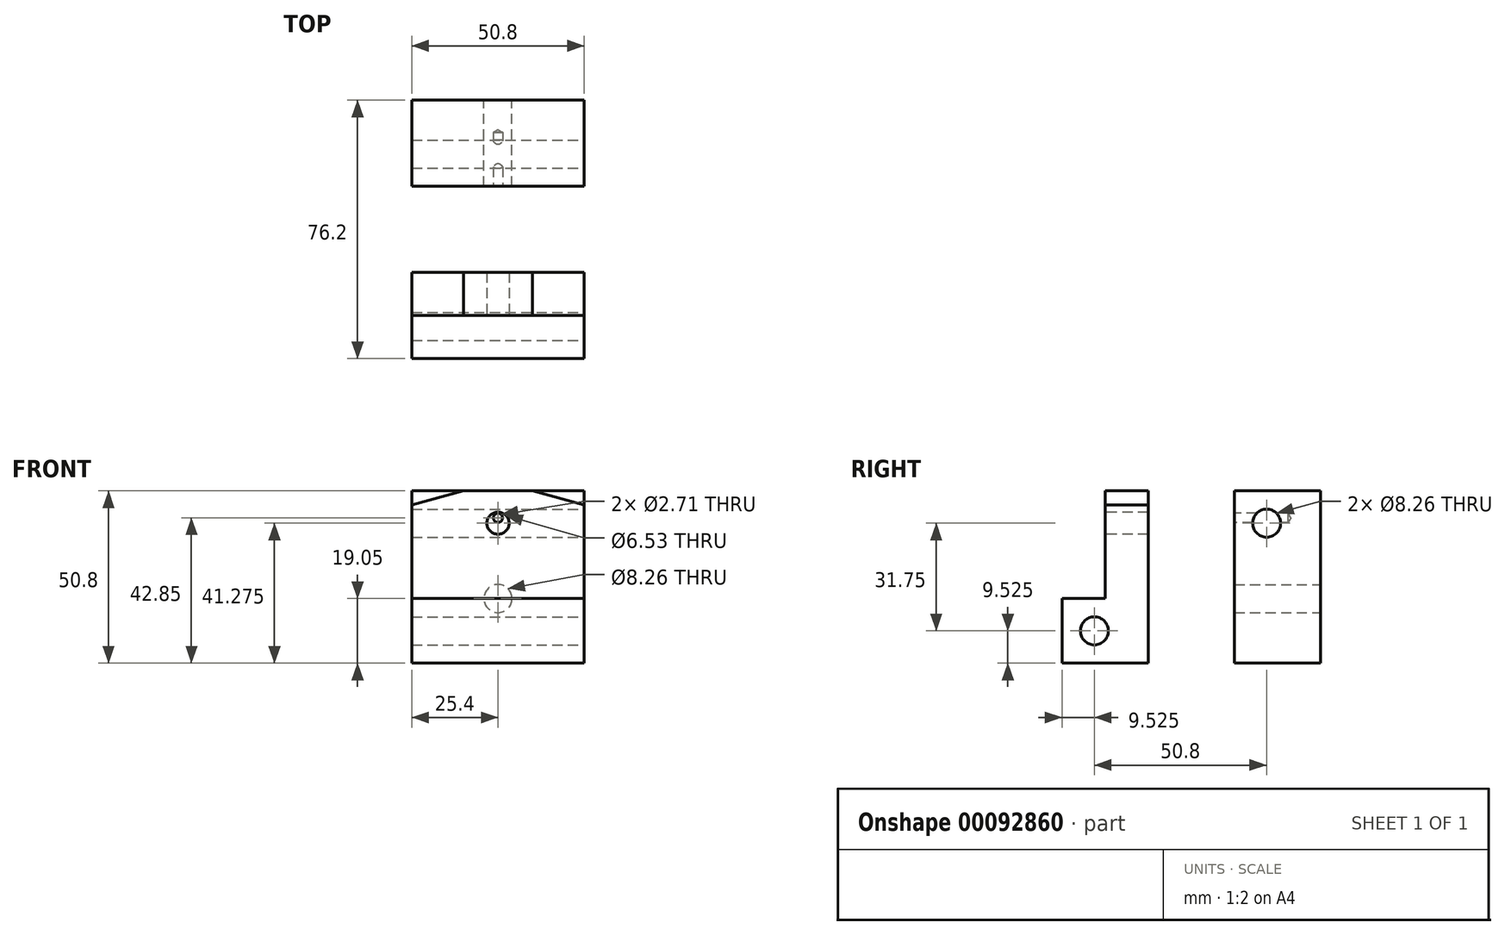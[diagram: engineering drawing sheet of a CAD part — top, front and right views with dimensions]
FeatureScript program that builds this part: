
annotation { "Feature Type Name" : "Feature", "Feature Type Description" : "" }
export const myFeature = defineFeature(function(context is Context, id is Id, definition is map)
    precondition{}
    {
        {
            var Q0;
            Q0=qCreatedBy(makeId("Front.planeOp"),FACE);
            var sketch = newSketch(context, id + "F0", { "sketchPlane" : qUnion([Q0])});
            skLineSegment(sketch, "E0.bottom", {"start": v(25.4, -25.4) * mm, "end": v(-25.4, -25.4) * mm});
            skLineSegment(sketch, "E0.top", {"start": v(25.4, 25.4) * mm, "end": v(-25.4, 25.4) * mm});
            skLineSegment(sketch, "E0.left", {"start": v(25.4, -25.4) * mm, "end": v(25.4, 25.4) * mm});
            skLineSegment(sketch, "E0.right", {"start": v(-25.4, -25.4) * mm, "end": v(-25.4, 25.4) * mm});
            skPoint(sketch, "E0.middle", {"position": v(0, 0) * mm});
            skLineSegment(sketch, "E1", {"start": v(-25.4, -6.35) * mm, "end": v(25.4, -6.35) * mm, "construction": true});
            skLineSegment(sketch, "E2", {"start": v(0, 25.4) * mm, "end": v(0, -25.4) * mm, "construction": true});
            skCircle(sketch, "E3", {"center": v(0, -6.35) * mm, "radius": 4.13 * mm});
            skSolve(sketch);
        }
        {
            var Q0;
            Q0=makeQuery(id+"F0.imprint","IMPRINT",FACE,{"disambiguationData":[TD([[makeQuery(id+"F0.imprint","IMPRINT",EDGE,{"derivedFrom":sQuery(id+"F0.wireOp",EDGE,"E0.bottom")}),-1.0]])]});
            extrude(context, id + "F1", {"entities" : qUnion([Q0]), "depth" : 25.4 * mm});
        }
        {
            var Q0;
            Q0=makeQuery(id+"F1.opExtrude","SWEPT_FACE",FACE,{"disambiguationData":[OSD([sQuery(id+"F0.wireOp",EDGE,"E0.left")])]});
            var sketch = newSketch(context, id + "F2", { "sketchPlane" : qUnion([Q0])});
            skLineSegment(sketch, "E4", {"start": v(-15.88, 25.4) * mm, "end": v(-15.87, -25.4) * mm, "construction": true});
            skLineSegment(sketch, "E5", {"start": v(-25.4, 15.88) * mm, "end": v(0, 15.88) * mm, "construction": true});
            skPoint(sketch, "E6", {"position": v(-15.88, 15.88) * mm});
            skSolve(sketch);
        }
        {
            var Q0;
            Q0=sQuery(id+"F2.wireOp",VERTEX,"E6");
            var Q1;
            Q1=makeQuery(id+"F1.opExtrude","SWEPT_BODY",BODY,{"disambiguationData":[OSD([sQuery(id+"F0.wireOp",EDGE,"E0.bottom"),sQuery(id+"F0.wireOp",EDGE,"E0.top"),sQuery(id+"F0.wireOp",EDGE,"E0.left"),sQuery(id+"F0.wireOp",EDGE,"E0.right"),sQuery(id+"F0.wireOp",EDGE,"E3")])]});
            hole(context, id + "F3", {"style" : HoleStyle.SIMPLE, "endStyle" : HoleEndStyle.THROUGH, "holeDiameter" : 8.25 * mm, "locations" : qUnion([Q0]), "scope" : qUnion([Q1]), "isTappedThrough" : true});
        }
        {
            var Q0;
            Q0=makeQuery(id+"F1.opExtrude","CAP_FACE",FACE,{"disambiguationData":[OSD([sQuery(id+"F0.wireOp",EDGE,"E0.bottom"),sQuery(id+"F0.wireOp",EDGE,"E0.top"),sQuery(id+"F0.wireOp",EDGE,"E0.left"),sQuery(id+"F0.wireOp",EDGE,"E0.right"),sQuery(id+"F0.wireOp",EDGE,"E3")])],"isStart":false});
            cPlane(context, id + "F4", {"entities" : qUnion([Q0]), "cplaneType" : CPlaneType.OFFSET, "offset" : 25.4 * mm, "width" : 152.4 * mm, "height" : 152.4 * mm});
        }
        {
            var Q0;
            Q0=qCreatedBy(id+"F4.planeOp",FACE);
            var sketch = newSketch(context, id + "F5", { "sketchPlane" : qUnion([Q0])});
            skLineSegment(sketch, "E7.0", {"start": v(10.16, 25.4) * mm, "end": v(-10.16, 25.4) * mm});
            skLineSegment(sketch, "E8.0", {"start": v(25.4, -25.4) * mm, "end": v(25.4, 21.32) * mm});
            skLineSegment(sketch, "E9.0", {"start": v(25.4, -25.4) * mm, "end": v(-25.4, -25.4) * mm});
            skLineSegment(sketch, "E10.0", {"start": v(-25.4, -25.4) * mm, "end": v(-25.4, 21.32) * mm});
            skLineSegment(sketch, "E11", {"start": v(0, 25.4) * mm, "end": v(0, -25.4) * mm, "construction": true});
            skLineSegment(sketch, "E12", {"start": v(-10.16, 25.4) * mm, "end": v(-10.16, -25.4) * mm, "construction": true});
            skLineSegment(sketch, "E13", {"start": v(-25.4, 15.87) * mm, "end": v(25.4, 15.88) * mm, "construction": true});
            skLineSegment(sketch, "E14", {"start": v(10.16, 25.4) * mm, "end": v(10.16, -25.4) * mm, "construction": true});
            skLineSegment(sketch, "E15", {"start": v(10.16, 25.4) * mm, "end": v(25.4, 21.32) * mm});
            skLineSegment(sketch, "E16", {"start": v(-10.16, 25.4) * mm, "end": v(-25.4, 21.32) * mm});
            skPoint(sketch, "E17", {"position": v(0, 15.88) * mm});
            skPoint(sketch, "E18.orphan", {"position": v(-25.4, 25.4) * mm});
            skPoint(sketch, "E19.orphan", {"position": v(25.4, 25.4) * mm});
            skSolve(sketch);
        }
        {
            var Q0;
            Q0=makeQuery(id+"F5.imprint","IMPRINT",FACE,{"disambiguationData":[TD([[makeQuery(id+"F5.imprint","IMPRINT",EDGE,{"derivedFrom":sQuery(id+"F5.wireOp",EDGE,"E7.0")}),1.0]])]});
            extrude(context, id + "F6", {"entities" : qUnion([Q0]), "depth" : 25.4 * mm});
        }
        {
            var Q0;
            Q0=makeQuery(id+"F6.opExtrude","CAP_FACE",FACE,{"disambiguationData":[OSD([sQuery(id+"F5.wireOp",EDGE,"E7.0"),sQuery(id+"F5.wireOp",EDGE,"E8.0"),sQuery(id+"F5.wireOp",EDGE,"E9.0"),sQuery(id+"F5.wireOp",EDGE,"E10.0"),sQuery(id+"F5.wireOp",EDGE,"E15"),sQuery(id+"F5.wireOp",EDGE,"E16")])],"isStart":false});
            var sketch = newSketch(context, id + "F7", { "sketchPlane" : qUnion([Q0])});
            skPoint(sketch, "E20.0", {"position": v(0, 15.88) * mm});
            skSolve(sketch);
        }
        {
            var Q0;
            Q0=sQuery(id+"F7.wireOp",VERTEX,"E20.0");
            var Q1;
            Q1=makeQuery(id+"F6.opExtrude","SWEPT_BODY",BODY,{"disambiguationData":[OSD([sQuery(id+"F5.wireOp",EDGE,"E7.0"),sQuery(id+"F5.wireOp",EDGE,"E8.0"),sQuery(id+"F5.wireOp",EDGE,"E9.0"),sQuery(id+"F5.wireOp",EDGE,"E10.0"),sQuery(id+"F5.wireOp",EDGE,"E15"),sQuery(id+"F5.wireOp",EDGE,"E16")])]});
            hole(context, id + "F8", {"style" : HoleStyle.SIMPLE, "endStyle" : HoleEndStyle.THROUGH, "standardTappedOrClearance" : lookupTablePath({ "standard" : "ANSI", "engagement" : "75%", "pitch" : "18 tpi", "size" : "5/16", "type" : "Tapped" }), "standardBlindInLast" : lookupTablePath({ "standard" : "ANSI", "engagement" : "75%", "pitch" : "18 tpi", "size" : "5/16", "type" : "Tapped" }), "holeDiameter" : 6.53 * mm, "locations" : qUnion([Q0]), "scope" : qUnion([Q1]), "isTappedThrough" : true, "majorDiameter" : 7.94 * mm, "showTappedDepth" : true});
        }
        {
            var Q0;
            Q0=makeQuery(id+"F6.opExtrude","SWEPT_FACE",FACE,{"disambiguationData":[OSD([sQuery(id+"F5.wireOp",EDGE,"E8.0")])]});
            var sketch = newSketch(context, id + "F9", { "sketchPlane" : qUnion([Q0])});
            skLineSegment(sketch, "E21.0", {"start": v(-76.2, 25.4) * mm, "end": v(-50.8, 25.4) * mm, "construction": true});
            skLineSegment(sketch, "E22.0", {"start": v(-76.2, -25.4) * mm, "end": v(-76.2, 21.32) * mm, "construction": true});
            skLineSegment(sketch, "E23.0", {"start": v(-76.2, 25.4) * mm, "end": v(-76.2, 21.32) * mm, "construction": true});
            skLineSegment(sketch, "E24.0", {"start": v(-76.2, -25.4) * mm, "end": v(-50.8, -25.4) * mm, "construction": true});
            skLineSegment(sketch, "E25.0", {"start": v(-50.8, -25.4) * mm, "end": v(-50.8, 21.32) * mm, "construction": true});
            skLineSegment(sketch, "E26.0.0", {"start": v(-50.8, 21.32) * mm, "end": v(-50.8, 25.4) * mm, "construction": true});
            skLineSegment(sketch, "E26.0.1", {"start": v(-50.8, 25.4) * mm, "end": v(-76.2, 25.4) * mm, "construction": true});
            skLineSegment(sketch, "E26.0.3", {"start": v(-76.2, 21.32) * mm, "end": v(-50.8, 21.32) * mm, "construction": true});
            skLineSegment(sketch, "E27", {"start": v(-63.5, 25.4) * mm, "end": v(-63.5, -25.4) * mm, "construction": true});
            skLineSegment(sketch, "E28", {"start": v(-76.2, -6.35) * mm, "end": v(-50.8, -6.35) * mm, "construction": true});
            skLineSegment(sketch, "E29.bottom", {"start": v(-76.2, 25.4) * mm, "end": v(-63.5, 25.4) * mm});
            skLineSegment(sketch, "E29.top", {"start": v(-76.2, -6.35) * mm, "end": v(-63.5, -6.35) * mm});
            skLineSegment(sketch, "E29.left", {"start": v(-76.2, 25.4) * mm, "end": v(-76.2, -6.35) * mm});
            skLineSegment(sketch, "E29.right", {"start": v(-63.5, 25.4) * mm, "end": v(-63.5, -6.35) * mm});
            skSolve(sketch);
        }
        {
            var Q0;
            {var subQ0=sQuery(id+"F9.wireOp",EDGE,"E29.top");Q0=makeQuery(id+"F9.imprint","IMPRINT",FACE,{"disambiguationData":[TD([[makeQuery(id+"F9.imprint","IMPRINT",EDGE,{"derivedFrom":subQ0}),1.0]])]});}
            var Q1;
            {var subQ0=sQuery(id+"F9.wireOp",EDGE,"E29.bottom");Q1=makeQuery(id+"F9.imprint","IMPRINT",FACE,{"disambiguationData":[TD([[makeQuery(id+"F9.imprint","IMPRINT",EDGE,{"derivedFrom":subQ0}),-1.0]])]});}
            extrude(context, id + "F10", {"entities" : qUnion([Q0, Q1]), "operationType" : NewBodyOperationType.REMOVE, "endBound" : BoundingType.THROUGH_ALL, "oppositeDirection" : true, "depth" : 25.4 * mm});
        }
        {
            var Q0;
            Q0=makeQuery(id+"F6.opExtrude","SWEPT_FACE",FACE,{"disambiguationData":[OSD([sQuery(id+"F5.wireOp",EDGE,"E8.0")])]});
            var sketch = newSketch(context, id + "F11", { "sketchPlane" : qUnion([Q0])});
            skLineSegment(sketch, "E30", {"start": v(-76.2, -15.88) * mm, "end": v(-50.8, -15.88) * mm, "construction": true});
            skLineSegment(sketch, "E31", {"start": v(-66.67, -6.35) * mm, "end": v(-66.67, -25.4) * mm, "construction": true});
            skPoint(sketch, "E32", {"position": v(-66.67, -15.88) * mm});
            skSolve(sketch);
        }
        {
            var Q0;
            Q0=sQuery(id+"F11.wireOp",VERTEX,"E32");
            var Q1;
            Q1=makeQuery(id+"F6.opExtrude","SWEPT_BODY",BODY,{"disambiguationData":[OSD([sQuery(id+"F5.wireOp",EDGE,"E7.0"),sQuery(id+"F5.wireOp",EDGE,"E8.0"),sQuery(id+"F5.wireOp",EDGE,"E9.0"),sQuery(id+"F5.wireOp",EDGE,"E10.0"),sQuery(id+"F5.wireOp",EDGE,"E15"),sQuery(id+"F5.wireOp",EDGE,"E16")])]});
            hole(context, id + "F12", {"style" : HoleStyle.SIMPLE, "endStyle" : HoleEndStyle.THROUGH, "holeDiameter" : 8.25 * mm, "locations" : qUnion([Q0]), "scope" : qUnion([Q1]), "isTappedThrough" : true});
        }
        {
            var Q0;
            Q0=makeQuery(id+"F1.opExtrude","CAP_FACE",FACE,{"disambiguationData":[OSD([sQuery(id+"F0.wireOp",EDGE,"E0.bottom"),sQuery(id+"F0.wireOp",EDGE,"E0.top"),sQuery(id+"F0.wireOp",EDGE,"E0.left"),sQuery(id+"F0.wireOp",EDGE,"E0.right"),sQuery(id+"F0.wireOp",EDGE,"E3")])],"isStart":false});
            var sketch = newSketch(context, id + "F13", { "sketchPlane" : qUnion([Q0])});
            skLineSegment(sketch, "E33.0.0", {"start": v(-25.4, -25.4) * mm, "end": v(25.4, -25.4) * mm, "construction": true});
            skLineSegment(sketch, "E33.0.1", {"start": v(25.4, -25.4) * mm, "end": v(25.4, 25.4) * mm, "construction": true});
            skLineSegment(sketch, "E33.0.2", {"start": v(25.4, 25.4) * mm, "end": v(-25.4, 25.4) * mm, "construction": true});
            skLineSegment(sketch, "E33.0.3", {"start": v(-25.4, 25.4) * mm, "end": v(-25.4, -25.4) * mm, "construction": true});
            skLineSegment(sketch, "E34", {"start": v(-25.4, 17.45) * mm, "end": v(25.4, 17.45) * mm});
            skPoint(sketch, "E35", {"position": v(0, 17.45) * mm});
            skSolve(sketch);
        }
        {
            var Q0;
            Q0=sQuery(id+"F13.wireOp",VERTEX,"E35");
            var Q1;
            Q1=makeQuery(id+"F1.opExtrude","SWEPT_BODY",BODY,{"disambiguationData":[OSD([sQuery(id+"F0.wireOp",EDGE,"E0.bottom"),sQuery(id+"F0.wireOp",EDGE,"E0.top"),sQuery(id+"F0.wireOp",EDGE,"E0.left"),sQuery(id+"F0.wireOp",EDGE,"E0.right"),sQuery(id+"F0.wireOp",EDGE,"E3")])]});
            hole(context, id + "F14", {"style" : HoleStyle.SIMPLE, "endStyle" : HoleEndStyle.BLIND, "standardTappedOrClearance" : lookupTablePath({ "standard" : "ANSI", "engagement" : "75%", "pitch" : "32 tpi", "size" : "#6", "type" : "Tapped" }), "standardBlindInLast" : lookupTablePath({ "standard" : "ANSI", "engagement" : "75%", "pitch" : "32 tpi", "size" : "#6", "type" : "Tapped" }), "holeDiameter" : 2.7 * mm, "holeDepth" : 15.88 * mm, "locations" : qUnion([Q0]), "scope" : qUnion([Q1]), "majorDiameter" : 3.5 * mm});
        }
    });
